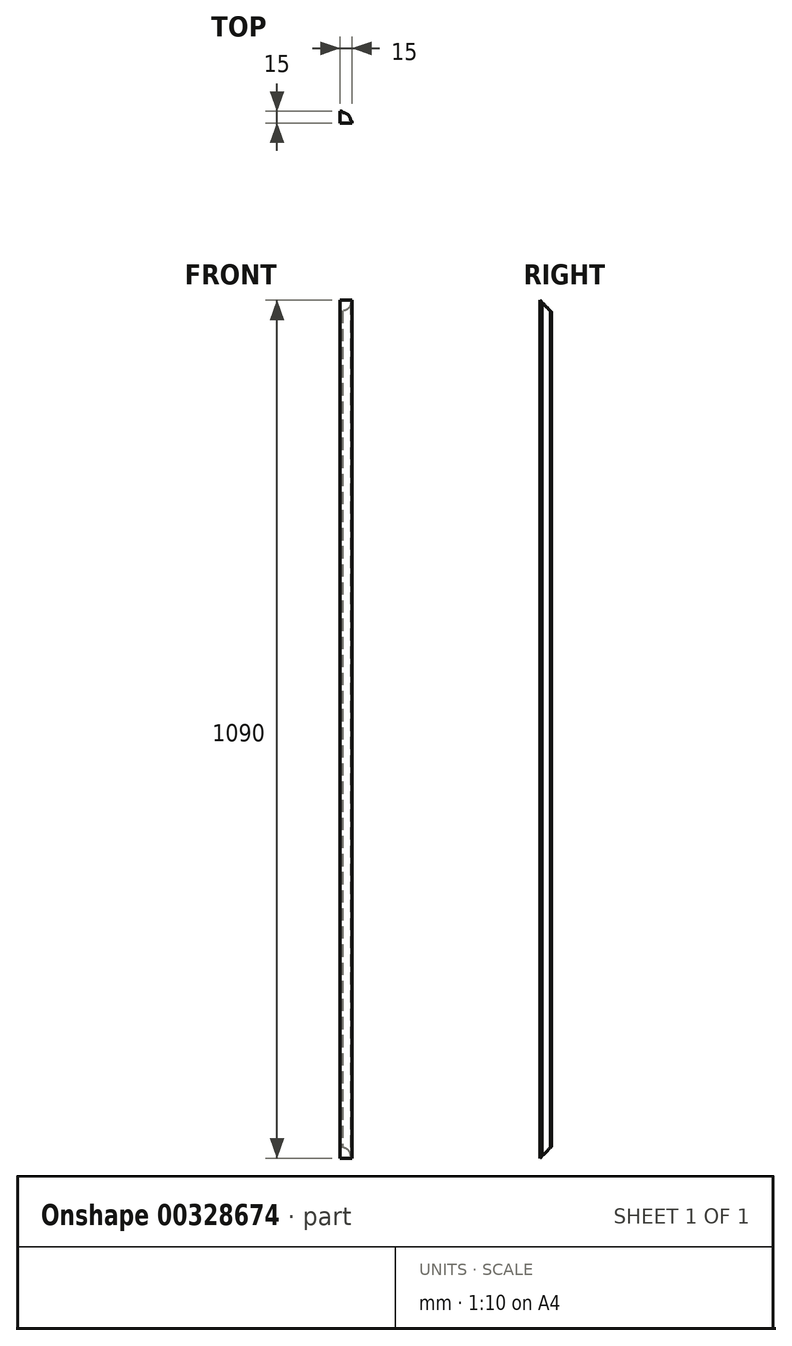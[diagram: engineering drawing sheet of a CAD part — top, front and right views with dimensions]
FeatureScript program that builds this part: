
annotation { "Feature Type Name" : "Feature", "Feature Type Description" : "" }
export const myFeature = defineFeature(function(context is Context, id is Id, definition is map)
    precondition{}
    {
        {
            var Q0;
            Q0=qCreatedBy(makeId("Top.planeOp"),FACE);
            var sketch = newSketch(context, id + "F0", { "sketchPlane" : qUnion([Q0])});
            skLineSegment(sketch, "E0", {"start": v(0, 0) * mm, "end": v(15, 0) * mm});
            skLineSegment(sketch, "E1", {"start": v(15, 0) * mm, "end": v(0, 0) * mm});
            skLineSegment(sketch, "E2", {"start": v(0, 15) * mm, "end": v(0, 0) * mm});
            skLineSegment(sketch, "E3", {"start": v(0, 15) * mm, "end": v(2, 15) * mm});
            skLineSegment(sketch, "E4", {"start": v(3, 14) * mm, "end": v(3, 13.5) * mm});
            skLineSegment(sketch, "E5", {"start": v(15, 0) * mm, "end": v(15, 2) * mm});
            skLineSegment(sketch, "E6", {"start": v(14, 3) * mm, "end": v(13.5, 3) * mm});
            skLineSegment(sketch, "E7", {"start": v(3, 13.5) * mm, "end": v(3, 3) * mm, "construction": true});
            skLineSegment(sketch, "E8", {"start": v(3, 3) * mm, "end": v(13.5, 3) * mm, "construction": true});
            skArc(sketch, "E9", {"start": v(13.5, 3) * mm, "mid": v(10.42, 10.42) * mm, "end": v(3, 13.5) * mm});
            skPoint(sketch, "E10.visualSharp", {"position": v(3, 15) * mm});
            skArc(sketch, "E10.filletArc", {"start": v(3, 14) * mm, "mid": v(2.7, 14.7) * mm, "end": v(2, 15) * mm});
            skPoint(sketch, "E11.visualSharp", {"position": v(15, 3) * mm});
            skArc(sketch, "E11.filletArc", {"start": v(15, 2) * mm, "mid": v(14.7, 2.7) * mm, "end": v(14, 3) * mm});
            skSolve(sketch);
        }
        {
            var Q0;
            Q0=qSketchRegion(id+"F0",true);
            extrude(context, id + "F1", {"entities" : qUnion([Q0]), "depth" : 1090 * mm});
        }
        {
            var Q0;
            Q0=makeQuery(id+"F1.opExtrude","SWEPT_FACE",FACE,{"disambiguationData":[OSD([sQuery(id+"F0.wireOp",EDGE,"E2")])]});
            var sketch = newSketch(context, id + "F2", { "sketchPlane" : qUnion([Q0])});
            skLineSegment(sketch, "E12", {"start": v(0, 0) * mm, "end": v(-15, 15) * mm});
            skLineSegment(sketch, "E13", {"start": v(-15, 15) * mm, "end": v(-15, 0) * mm});
            skLineSegment(sketch, "E14", {"start": v(-15, 0) * mm, "end": v(0, 0) * mm});
            skLineSegment(sketch, "E15", {"start": v(0, 1090) * mm, "end": v(-15, 1075) * mm});
            skLineSegment(sketch, "E16", {"start": v(-15, 1075) * mm, "end": v(-15, 1090) * mm});
            skLineSegment(sketch, "E17", {"start": v(-15, 1090) * mm, "end": v(0, 1090) * mm});
            skSolve(sketch);
        }
        {
            var Q0;
            Q0=qSketchRegion(id+"F2",true);
            extrude(context, id + "F3", {"entities" : qUnion([Q0]), "operationType" : NewBodyOperationType.REMOVE, "oppositeDirection" : true, "depth" : 25 * mm});
        }
    });
